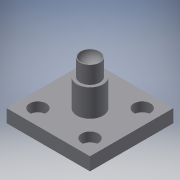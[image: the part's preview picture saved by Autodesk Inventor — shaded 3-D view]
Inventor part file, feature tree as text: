
AUTODESK INVENTOR PART (.ipt)
format: ipt  version: 2017 (Build 210142000, 142)  size: 167,936 bytes
history: native  units: in
note: dims shown in document units (in); Inventor stores cm internally (conversion verified against a paired STEP export)
features: hole x5, sketch x4, revolve x1, plane x1, extrude x1
ambient origin geometry x8: Origin, YZ Plane, XZ Plane, XY Plane, X Axis, Y Axis, Z Axis, Center Point
bodies: Solid1 (feature_tree)
feature tree (12):
  sketch  "Sketch1"  dims[d11=0.02in d13=90.0deg]
  revolve  "Revolution1"  Angle=90.0deg
  plane  "Work Plane1"
  hole  "Hole7"  [1 undecoded]
  hole  "Hole8"  [1 undecoded]
  hole  "Hole9"  [1 undecoded]
  hole  "Hole10"  [1 undecoded]
  extrude  "Extrusion3"  Depth=0.1772in
  sketch  "3D Sketch1"
  hole  "Hole11"  [1 undecoded]
  sketch  "Sketch4"  dims[d72=1.0in d73=1.0in d74=0.313in d75=0.236in d76=0.0246in d77=0.329in d78=0.375in d79=0.25in d80=0.5635in d81=0.5in d82=0.8108in]
  sketch  "Sketch8"  dims[d140=0.3937in d141=0.3937in d85=0.125in d86=0.236in d87=0.375in d88=0.25in d89=0.5635in d90=0.8in d91=0.8108in d138=0.3937in d139=0.3937in d94=0.04in d95=0.236in d96=0.375in d97=0.25in d98=0.5635in d99=0.1in d100=0.8108in d142=0.3937in d143=0.3937in d103=0.062in d104=0.236in d105=0.375in d106=0.25in d107=0.5635in d108=0.5in d109=0.8108in d115=1.6in d116=1.6in d117=0.25in d118=0.0in d123=0.196in d124=0.75in d125=0.318in d126=0.18in d127=0.5635in d128=1.0in d129=0.8108in d131=0.25in d136=0.1772in d137=0.5841in]
note: 5 required parameter values undecoded (feature->parameter linkage not recoverable at this tier; creation-order binding heuristic only, values carry confidence <= 0.55)
